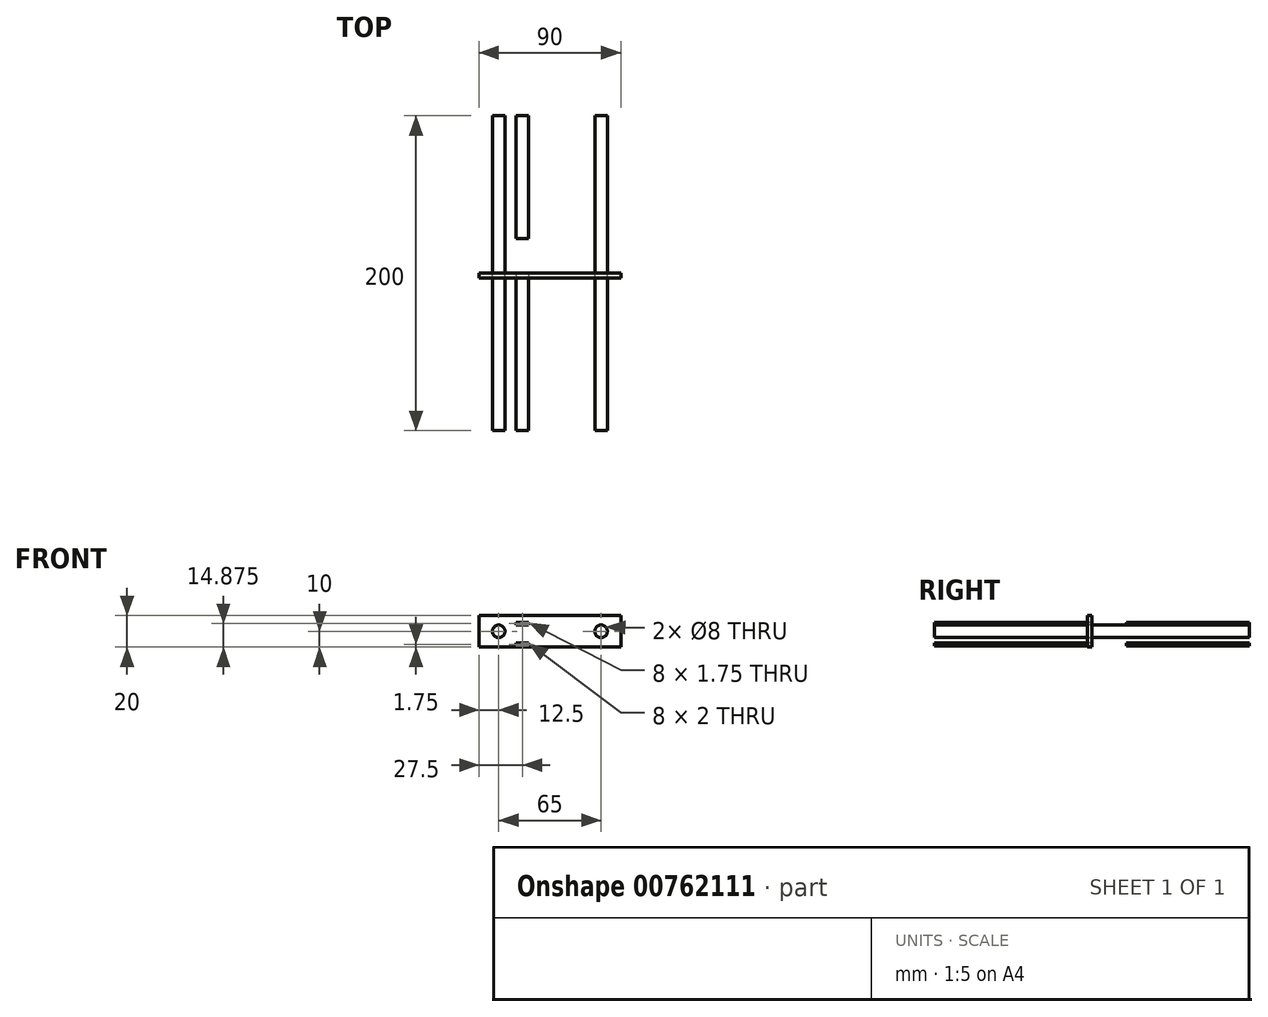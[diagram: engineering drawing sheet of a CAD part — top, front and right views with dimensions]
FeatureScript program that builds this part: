
annotation { "Feature Type Name" : "Feature", "Feature Type Description" : "" }
export const myFeature = defineFeature(function(context is Context, id is Id, definition is map)
    precondition{}
    {
        {
            var Q0;
            Q0=qCreatedBy(makeId("Front.planeOp"),FACE);
            var sketch = newSketch(context, id + "F0", { "sketchPlane" : qUnion([Q0])});
            skCircle(sketch, "E0", {"center": v(-32.5, 0) * mm, "radius": 4 * mm});
            skCircle(sketch, "E1", {"center": v(32.5, 0) * mm, "radius": 4 * mm});
            skLineSegment(sketch, "E2", {"start": v(-32.5, 0) * mm, "end": v(32.5, 0) * mm, "construction": true});
            skLineSegment(sketch, "E3.bottom", {"start": v(-21.5, 4) * mm, "end": v(-13.5, 4) * mm});
            skLineSegment(sketch, "E3.top", {"start": v(-21.5, 5.75) * mm, "end": v(-13.5, 5.75) * mm});
            skLineSegment(sketch, "E3.left", {"start": v(-21.5, 4) * mm, "end": v(-21.5, 5.75) * mm});
            skLineSegment(sketch, "E3.right", {"start": v(-13.5, 4) * mm, "end": v(-13.5, 5.75) * mm});
            skLineSegment(sketch, "E4.bottom", {"start": v(-21.5, -7.25) * mm, "end": v(-13.5, -7.25) * mm});
            skLineSegment(sketch, "E4.top", {"start": v(-21.5, -9.25) * mm, "end": v(-13.5, -9.25) * mm});
            skLineSegment(sketch, "E4.left", {"start": v(-21.5, -7.25) * mm, "end": v(-21.5, -9.25) * mm});
            skLineSegment(sketch, "E4.right", {"start": v(-13.5, -7.25) * mm, "end": v(-13.5, -9.25) * mm});
            skPoint(sketch, "E5", {"position": v(-28.5, 0) * mm});
            skPoint(sketch, "E6", {"position": v(0, 0) * mm});
            skLineSegment(sketch, "E7", {"start": v(-32.5, 0) * mm, "end": v(-32.5, 4) * mm, "construction": true});
            skSolve(sketch);
        }
        {
            var Q0;
            Q0=makeQuery(id+"F0.imprint","IMPRINT",FACE,{"disambiguationData":[TD([[makeQuery(id+"F0.imprint","IMPRINT",EDGE,{"derivedFrom":sQuery(id+"F0.wireOp",EDGE,"E0")}),1.0]])]});
            var Q1;
            Q1=makeQuery(id+"F0.imprint","IMPRINT",FACE,{"disambiguationData":[TD([[makeQuery(id+"F0.imprint","IMPRINT",EDGE,{"derivedFrom":sQuery(id+"F0.wireOp",EDGE,"E3.bottom")}),1.0]])]});
            var Q2;
            Q2=makeQuery(id+"F0.imprint","IMPRINT",FACE,{"disambiguationData":[TD([[makeQuery(id+"F0.imprint","IMPRINT",EDGE,{"derivedFrom":sQuery(id+"F0.wireOp",EDGE,"E4.bottom")}),-1.0]])]});
            var Q3;
            Q3=makeQuery(id+"F0.imprint","IMPRINT",FACE,{"disambiguationData":[TD([[makeQuery(id+"F0.imprint","IMPRINT",EDGE,{"derivedFrom":sQuery(id+"F0.wireOp",EDGE,"E1")}),1.0]])]});
            extrude(context, id + "F1", {"entities" : qUnion([Q0, Q1, Q2, Q3]), "endBound" : BoundingType.SYMMETRIC, "depth" : 200 * mm, "offsetDistance" : 25 * mm});
        }
        {
            var Q0;
            Q0=qCreatedBy(makeId("Front.planeOp"),FACE);
            var sketch = newSketch(context, id + "F2", { "sketchPlane" : qUnion([Q0])});
            skLineSegment(sketch, "E8.bottom", {"start": v(-45, -10) * mm, "end": v(45, -10) * mm});
            skLineSegment(sketch, "E8.top", {"start": v(-45, 10) * mm, "end": v(45, 10) * mm});
            skLineSegment(sketch, "E8.left", {"start": v(-45, -10) * mm, "end": v(-45, 10) * mm});
            skLineSegment(sketch, "E8.right", {"start": v(45, -10) * mm, "end": v(45, 10) * mm});
            skCircle(sketch, "E9", {"center": v(-32.5, 0) * mm, "radius": 4 * mm});
            skCircle(sketch, "E10", {"center": v(32.5, 0) * mm, "radius": 4 * mm});
            skLineSegment(sketch, "E11", {"start": v(-32.5, 0) * mm, "end": v(32.5, 0) * mm, "construction": true});
            skPoint(sketch, "E12", {"position": v(45, 0) * mm});
            skPoint(sketch, "E13", {"position": v(0, -10) * mm});
            skPoint(sketch, "E14", {"position": v(0, 0) * mm});
            skSolve(sketch);
        }
        {
            var Q0;
            Q0=makeQuery(id+"F2.imprint","IMPRINT",FACE,{"disambiguationData":[TD([[makeQuery(id+"F2.imprint","IMPRINT",EDGE,{"derivedFrom":sQuery(id+"F2.wireOp",EDGE,"E8.bottom")}),1.0]])]});
            extrude(context, id + "F3", {"entities" : qUnion([Q0]), "depth" : 3 * mm, "offsetDistance" : 25 * mm});
        }
        {
            var Q0;
            Q0=makeQuery(id+"F3.opExtrude","CAP_FACE",FACE,{"disambiguationData":[OSD([sQuery(id+"F2.wireOp",EDGE,"E8.bottom"),sQuery(id+"F2.wireOp",EDGE,"E8.top"),sQuery(id+"F2.wireOp",EDGE,"E8.left"),sQuery(id+"F2.wireOp",EDGE,"E8.right"),sQuery(id+"F2.wireOp",EDGE,"E9"),sQuery(id+"F2.wireOp",EDGE,"E10")])],"isStart":false});
            var sketch = newSketch(context, id + "F4", { "sketchPlane" : qUnion([Q0])});
            skLineSegment(sketch, "E15.0.0", {"start": v(-13.5, 5.75) * mm, "end": v(-21.5, 5.75) * mm});
            skLineSegment(sketch, "E15.0.1", {"start": v(-21.5, 5.75) * mm, "end": v(-21.5, 4) * mm});
            skLineSegment(sketch, "E15.0.2", {"start": v(-21.5, 4) * mm, "end": v(-13.5, 4) * mm});
            skLineSegment(sketch, "E15.0.3", {"start": v(-13.5, 4) * mm, "end": v(-13.5, 5.75) * mm});
            skLineSegment(sketch, "E16.0.0", {"start": v(-21.5, -7.25) * mm, "end": v(-21.5, -9.25) * mm});
            skLineSegment(sketch, "E16.0.1", {"start": v(-21.5, -9.25) * mm, "end": v(-13.5, -9.25) * mm});
            skLineSegment(sketch, "E16.0.2", {"start": v(-13.5, -9.25) * mm, "end": v(-13.5, -7.25) * mm});
            skLineSegment(sketch, "E16.0.3", {"start": v(-13.5, -7.25) * mm, "end": v(-21.5, -7.25) * mm});
            skSolve(sketch);
        }
        {
            var Q0;
            Q0=makeQuery(id+"F4.imprint","IMPRINT",FACE,{"disambiguationData":[TD([[makeQuery(id+"F4.imprint","IMPRINT",EDGE,{"derivedFrom":sQuery(id+"F4.wireOp",EDGE,"E15.0.0")}),1.0]])]});
            var Q1;
            Q1=makeQuery(id+"F4.imprint","IMPRINT",FACE,{"disambiguationData":[TD([[makeQuery(id+"F4.imprint","IMPRINT",EDGE,{"derivedFrom":sQuery(id+"F4.wireOp",EDGE,"E16.0.0")}),1.0]])]});
            extrude(context, id + "F5", {"entities" : qUnion([Q0, Q1]), "operationType" : NewBodyOperationType.REMOVE, "oppositeDirection" : true, "depth" : 25 * mm, "offsetDistance" : 25 * mm});
        }
    });
